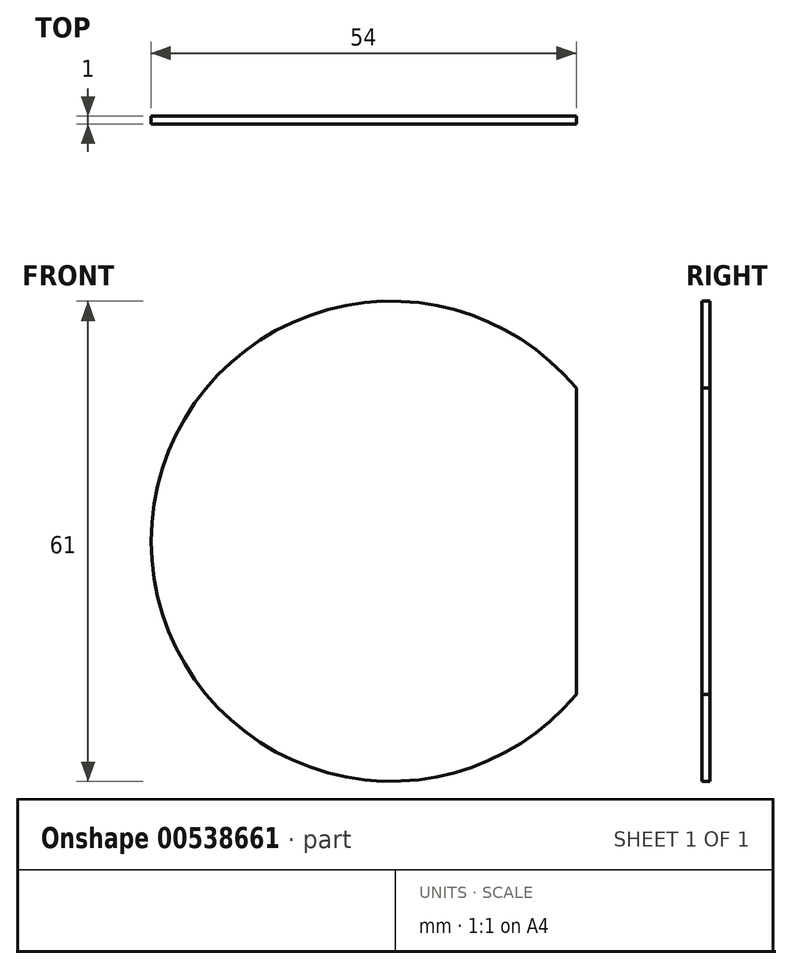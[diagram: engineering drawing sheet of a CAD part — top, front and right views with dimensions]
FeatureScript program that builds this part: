
annotation { "Feature Type Name" : "Feature", "Feature Type Description" : "" }
export const myFeature = defineFeature(function(context is Context, id is Id, definition is map)
    precondition{}
    {
        {
            var Q0;
            Q0=qCreatedBy(makeId("Front.planeOp"),FACE);
            var sketch = newSketch(context, id + "F0", { "sketchPlane" : qUnion([Q0])});
            skArc(sketch, "E0", {"start": v(23.5, 19.44) * mm, "mid": v(-30.5, 0) * mm, "end": v(23.5, -19.44) * mm});
            skLineSegment(sketch, "E1", {"start": v(23.5, 19.44) * mm, "end": v(23.5, -19.44) * mm});
            skSolve(sketch);
        }
        {
            var Q0;
            Q0=makeQuery(id+"F0.imprint","IMPRINT",FACE,{"disambiguationData":[TD([[makeQuery(id+"F0.imprint","IMPRINT",EDGE,{"derivedFrom":sQuery(id+"F0.wireOp",EDGE,"E0")}),1.0]])]});
            extrude(context, id + "F1", {"entities" : qUnion([Q0]), "depth" : 1 * mm, "offsetDistance" : 25 * mm});
        }
    });
